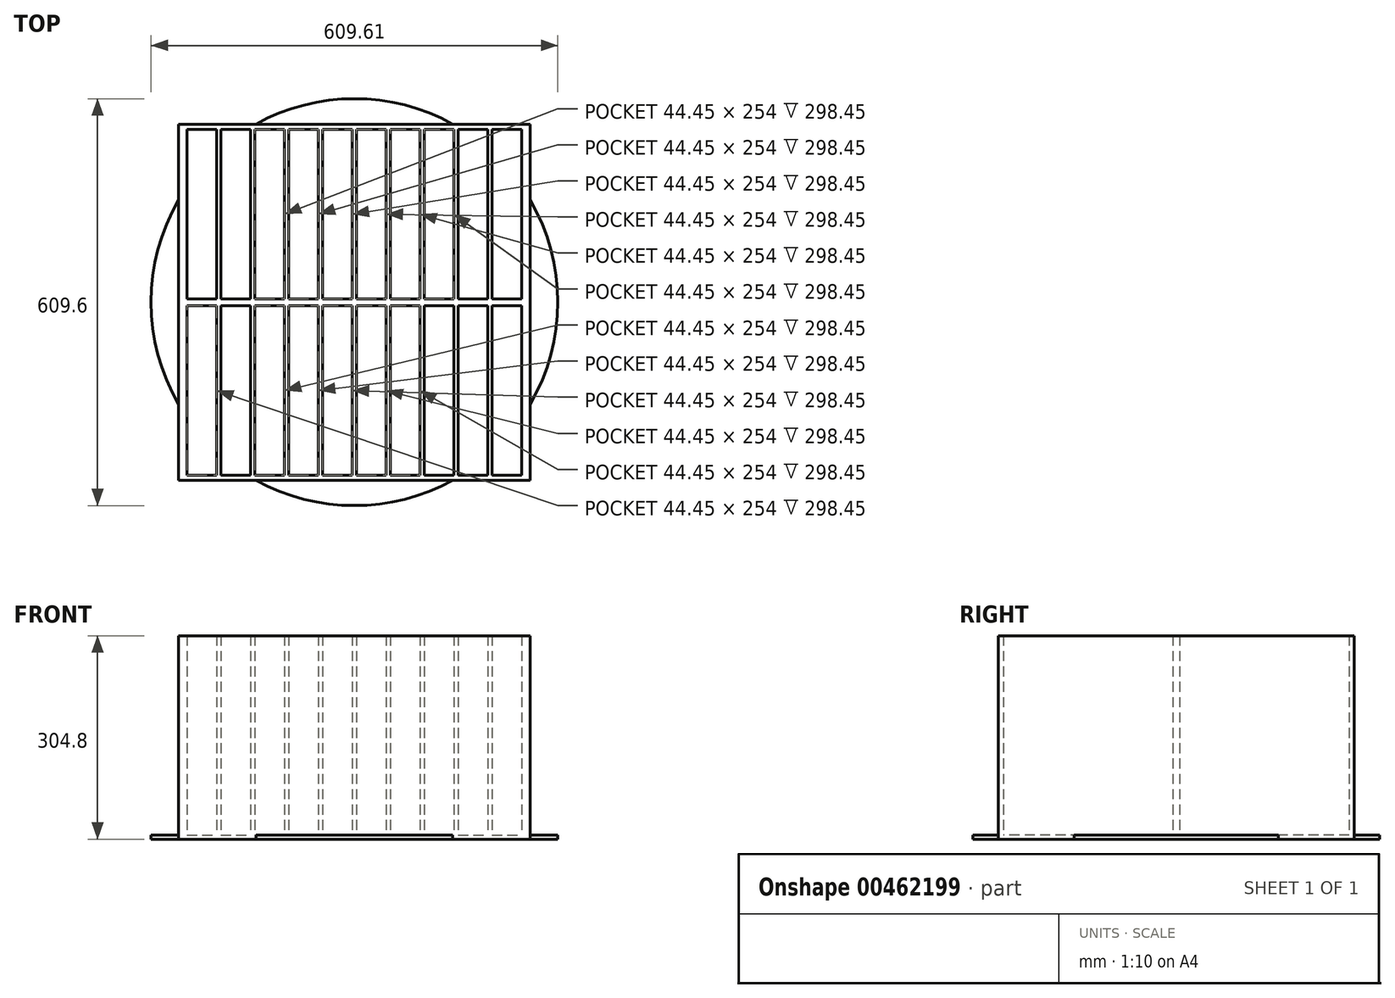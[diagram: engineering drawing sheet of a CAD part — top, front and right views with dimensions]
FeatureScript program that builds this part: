
annotation { "Feature Type Name" : "Feature", "Feature Type Description" : "" }
export const myFeature = defineFeature(function(context is Context, id is Id, definition is map)
    precondition{}
    {
        {
            var Q0;
            Q0=qCreatedBy(makeId("Top.planeOp"),FACE);
            var sketch = newSketch(context, id + "F0", { "sketchPlane" : qUnion([Q0])});
            skLineSegment(sketch, "E0.bottom", {"start": v(-260.35, 261.62) * mm, "end": v(266.7, 261.62) * mm});
            skLineSegment(sketch, "E0.top", {"start": v(-260.35, -271.78) * mm, "end": v(266.7, -271.78) * mm});
            skLineSegment(sketch, "E0.left", {"start": v(-260.35, 261.62) * mm, "end": v(-260.35, -271.78) * mm});
            skLineSegment(sketch, "E0.right", {"start": v(266.7, 261.62) * mm, "end": v(266.7, -271.78) * mm});
            skLineSegment(sketch, "E1.bottom", {"start": v(-247.65, 254) * mm, "end": v(-203.2, 254) * mm});
            skLineSegment(sketch, "E1.top", {"start": v(-247.65, 0) * mm, "end": v(-203.2, 0) * mm});
            skLineSegment(sketch, "E1.left", {"start": v(-247.65, 254) * mm, "end": v(-247.65, 0) * mm});
            skLineSegment(sketch, "E1.right", {"start": v(-203.2, 254) * mm, "end": v(-203.2, 0) * mm});
            skLineSegment(sketch, "E2.bottom", {"start": v(-196.85, 254) * mm, "end": v(-152.4, 254) * mm});
            skLineSegment(sketch, "E2.top", {"start": v(-196.85, 0) * mm, "end": v(-152.4, 0) * mm});
            skLineSegment(sketch, "E2.left", {"start": v(-196.85, 254) * mm, "end": v(-196.85, 0) * mm});
            skLineSegment(sketch, "E2.right", {"start": v(-152.4, 254) * mm, "end": v(-152.4, 0) * mm});
            skLineSegment(sketch, "E3.bottom", {"start": v(-146.05, 254) * mm, "end": v(-101.6, 254) * mm});
            skLineSegment(sketch, "E3.top", {"start": v(-146.05, 0) * mm, "end": v(-101.6, 0) * mm});
            skLineSegment(sketch, "E3.left", {"start": v(-146.05, 254) * mm, "end": v(-146.05, 0) * mm});
            skLineSegment(sketch, "E3.right", {"start": v(-101.6, 254) * mm, "end": v(-101.6, 0) * mm});
            skLineSegment(sketch, "E4.bottom", {"start": v(-95.25, 254) * mm, "end": v(-50.8, 254) * mm});
            skLineSegment(sketch, "E4.top", {"start": v(-95.25, 0) * mm, "end": v(-50.8, 0) * mm});
            skLineSegment(sketch, "E4.left", {"start": v(-95.25, 254) * mm, "end": v(-95.25, 0) * mm});
            skLineSegment(sketch, "E4.right", {"start": v(-50.8, 254) * mm, "end": v(-50.8, 0) * mm});
            skLineSegment(sketch, "E5.bottom", {"start": v(-44.45, 254) * mm, "end": v(0, 254) * mm});
            skLineSegment(sketch, "E5.top", {"start": v(-44.45, 0) * mm, "end": v(0, 0) * mm});
            skLineSegment(sketch, "E5.left", {"start": v(-44.45, 254) * mm, "end": v(-44.45, 0) * mm});
            skLineSegment(sketch, "E5.right", {"start": v(0, 254) * mm, "end": v(0, 0) * mm});
            skLineSegment(sketch, "E6.bottom", {"start": v(6.35, 254) * mm, "end": v(50.8, 254) * mm});
            skLineSegment(sketch, "E6.top", {"start": v(6.35, 0) * mm, "end": v(50.8, 0) * mm});
            skLineSegment(sketch, "E6.left", {"start": v(6.35, 254) * mm, "end": v(6.35, 0) * mm});
            skLineSegment(sketch, "E6.right", {"start": v(50.8, 254) * mm, "end": v(50.8, 0) * mm});
            skLineSegment(sketch, "E7.bottom", {"start": v(57.15, 254) * mm, "end": v(101.6, 254) * mm});
            skLineSegment(sketch, "E7.top", {"start": v(57.15, 0) * mm, "end": v(101.6, 0) * mm});
            skLineSegment(sketch, "E7.left", {"start": v(57.15, 254) * mm, "end": v(57.15, 0) * mm});
            skLineSegment(sketch, "E7.right", {"start": v(101.6, 254) * mm, "end": v(101.6, 0) * mm});
            skLineSegment(sketch, "E8.bottom", {"start": v(107.95, 254) * mm, "end": v(152.4, 254) * mm});
            skLineSegment(sketch, "E8.top", {"start": v(107.95, 0) * mm, "end": v(152.4, 0) * mm});
            skLineSegment(sketch, "E8.left", {"start": v(107.95, 254) * mm, "end": v(107.95, 0) * mm});
            skLineSegment(sketch, "E8.right", {"start": v(152.4, 254) * mm, "end": v(152.4, 0) * mm});
            skLineSegment(sketch, "E9.bottom", {"start": v(158.75, 254) * mm, "end": v(203.2, 254) * mm});
            skLineSegment(sketch, "E9.top", {"start": v(158.75, 0) * mm, "end": v(203.2, 0) * mm});
            skLineSegment(sketch, "E9.left", {"start": v(158.75, 254) * mm, "end": v(158.75, 0) * mm});
            skLineSegment(sketch, "E9.right", {"start": v(203.2, 254) * mm, "end": v(203.2, 0) * mm});
            skLineSegment(sketch, "E10.bottom", {"start": v(209.55, 254) * mm, "end": v(254, 254) * mm});
            skLineSegment(sketch, "E10.top", {"start": v(209.55, 0) * mm, "end": v(254, 0) * mm});
            skLineSegment(sketch, "E10.left", {"start": v(209.55, 254) * mm, "end": v(209.55, 0) * mm});
            skLineSegment(sketch, "E10.right", {"start": v(254, 254) * mm, "end": v(254, 0) * mm});
            skLineSegment(sketch, "E11.bottom", {"start": v(-247.65, -10.16) * mm, "end": v(-203.2, -10.16) * mm});
            skLineSegment(sketch, "E11.top", {"start": v(-247.65, -264.16) * mm, "end": v(-203.2, -264.16) * mm});
            skLineSegment(sketch, "E11.left", {"start": v(-247.65, -10.16) * mm, "end": v(-247.65, -264.16) * mm});
            skLineSegment(sketch, "E11.right", {"start": v(-203.2, -10.16) * mm, "end": v(-203.2, -264.16) * mm});
            skLineSegment(sketch, "E12.bottom", {"start": v(-196.85, -10.16) * mm, "end": v(-152.4, -10.16) * mm});
            skLineSegment(sketch, "E12.top", {"start": v(-196.85, -264.16) * mm, "end": v(-152.4, -264.16) * mm});
            skLineSegment(sketch, "E12.left", {"start": v(-196.85, -10.16) * mm, "end": v(-196.85, -264.16) * mm});
            skLineSegment(sketch, "E12.right", {"start": v(-152.4, -10.16) * mm, "end": v(-152.4, -264.16) * mm});
            skLineSegment(sketch, "E13.bottom", {"start": v(-146.05, -10.16) * mm, "end": v(-101.6, -10.16) * mm});
            skLineSegment(sketch, "E13.top", {"start": v(-146.05, -264.16) * mm, "end": v(-101.6, -264.16) * mm});
            skLineSegment(sketch, "E13.left", {"start": v(-146.05, -10.16) * mm, "end": v(-146.05, -264.16) * mm});
            skLineSegment(sketch, "E13.right", {"start": v(-101.6, -10.16) * mm, "end": v(-101.6, -264.16) * mm});
            skLineSegment(sketch, "E14.bottom", {"start": v(-95.25, -10.16) * mm, "end": v(-50.8, -10.16) * mm});
            skLineSegment(sketch, "E14.top", {"start": v(-95.25, -264.16) * mm, "end": v(-50.8, -264.16) * mm});
            skLineSegment(sketch, "E14.left", {"start": v(-95.25, -10.16) * mm, "end": v(-95.25, -264.16) * mm});
            skLineSegment(sketch, "E14.right", {"start": v(-50.8, -10.16) * mm, "end": v(-50.8, -264.16) * mm});
            skLineSegment(sketch, "E15.bottom", {"start": v(-44.45, -10.16) * mm, "end": v(0, -10.16) * mm});
            skLineSegment(sketch, "E15.top", {"start": v(-44.45, -264.16) * mm, "end": v(0, -264.16) * mm});
            skLineSegment(sketch, "E15.left", {"start": v(-44.45, -10.16) * mm, "end": v(-44.45, -264.16) * mm});
            skLineSegment(sketch, "E15.right", {"start": v(0, -10.16) * mm, "end": v(0, -264.16) * mm});
            skLineSegment(sketch, "E16.bottom", {"start": v(6.35, -10.16) * mm, "end": v(50.8, -10.16) * mm});
            skLineSegment(sketch, "E16.top", {"start": v(6.35, -264.16) * mm, "end": v(50.8, -264.16) * mm});
            skLineSegment(sketch, "E16.left", {"start": v(6.35, -10.16) * mm, "end": v(6.35, -264.16) * mm});
            skLineSegment(sketch, "E16.right", {"start": v(50.8, -10.16) * mm, "end": v(50.8, -264.16) * mm});
            skLineSegment(sketch, "E17.bottom", {"start": v(57.15, -10.16) * mm, "end": v(101.6, -10.16) * mm});
            skLineSegment(sketch, "E17.top", {"start": v(57.15, -264.16) * mm, "end": v(101.6, -264.16) * mm});
            skLineSegment(sketch, "E17.left", {"start": v(57.15, -10.16) * mm, "end": v(57.15, -264.16) * mm});
            skLineSegment(sketch, "E17.right", {"start": v(101.6, -10.16) * mm, "end": v(101.6, -264.16) * mm});
            skLineSegment(sketch, "E18.bottom", {"start": v(107.95, -10.16) * mm, "end": v(152.4, -10.16) * mm});
            skLineSegment(sketch, "E18.top", {"start": v(107.95, -264.16) * mm, "end": v(152.4, -264.16) * mm});
            skLineSegment(sketch, "E18.left", {"start": v(107.95, -10.16) * mm, "end": v(107.95, -264.16) * mm});
            skLineSegment(sketch, "E18.right", {"start": v(152.4, -10.16) * mm, "end": v(152.4, -264.16) * mm});
            skLineSegment(sketch, "E19.bottom", {"start": v(158.75, -10.16) * mm, "end": v(203.2, -10.16) * mm});
            skLineSegment(sketch, "E19.top", {"start": v(158.75, -264.16) * mm, "end": v(203.2, -264.16) * mm});
            skLineSegment(sketch, "E19.left", {"start": v(158.75, -10.16) * mm, "end": v(158.75, -264.16) * mm});
            skLineSegment(sketch, "E19.right", {"start": v(203.2, -10.16) * mm, "end": v(203.2, -264.16) * mm});
            skLineSegment(sketch, "E20.bottom", {"start": v(209.55, -10.16) * mm, "end": v(254, -10.16) * mm});
            skLineSegment(sketch, "E20.top", {"start": v(209.55, -264.16) * mm, "end": v(254, -264.16) * mm});
            skLineSegment(sketch, "E20.left", {"start": v(209.55, -10.16) * mm, "end": v(209.55, -264.16) * mm});
            skLineSegment(sketch, "E20.right", {"start": v(254, -10.16) * mm, "end": v(254, -264.16) * mm});
            skLineSegment(sketch, "E21", {"start": v(3.18, 261.62) * mm, "end": v(3.18, -271.78) * mm, "construction": true});
            skLineSegment(sketch, "E22", {"start": v(266.7, -5.08) * mm, "end": v(-260.35, -5.08) * mm, "construction": true});
            skCircle(sketch, "E23", {"center": v(3.18, -5.08) * mm, "radius": 304.8 * mm});
            skSolve(sketch);
        }
        {
            var Q0;
            {var subQ0=sQuery(id+"F0.wireOp",EDGE,"E11.top");Q0=makeQuery(id+"F0.imprint","IMPRINT",FACE,{"disambiguationData":[TD([[makeQuery(id+"F0.imprint","IMPRINT",EDGE,{"derivedFrom":subQ0}),-1.0]])]});}
            var Q1;
            {var subQ19=sQuery(id+"F0.wireOp",EDGE,"E1.top");Q1=makeQuery(id+"F0.imprint","IMPRINT",FACE,{"disambiguationData":[TD([[makeQuery(id+"F0.imprint","IMPRINT",EDGE,{"derivedFrom":subQ19}),-1.0]])]});}
            var Q2;
            {var subQ1=sQuery(id+"F0.wireOp",EDGE,"E1.bottom");Q2=makeQuery(id+"F0.imprint","IMPRINT",FACE,{"disambiguationData":[TD([[makeQuery(id+"F0.imprint","IMPRINT",EDGE,{"derivedFrom":subQ1}),1.0]])]});}
            var Q3;
            {var subQ13=sQuery(id+"F0.wireOp",EDGE,"E10.bottom");Q3=makeQuery(id+"F0.imprint","IMPRINT",FACE,{"disambiguationData":[TD([[makeQuery(id+"F0.imprint","IMPRINT",EDGE,{"derivedFrom":subQ13}),1.0]])]});}
            var Q4;
            {var subQ11=sQuery(id+"F0.wireOp",EDGE,"E20.top");Q4=makeQuery(id+"F0.imprint","IMPRINT",FACE,{"disambiguationData":[TD([[makeQuery(id+"F0.imprint","IMPRINT",EDGE,{"derivedFrom":subQ11}),-1.0]])]});}
            extrude(context, id + "F1", {"entities" : qUnion([Q0, Q1, Q2, Q3, Q4]), "depth" : 304.8 * mm, "offsetDistance" : 25.4 * mm});
        }
        {
            var Q0;
            {var subQ0=sQuery(id+"F0.wireOp",EDGE,"E23");var subQ1=sQuery(id+"F0.wireOp",EDGE,"E0.left");var subQ2=makeQuery(id+"F0.imprint","INTERSECT",VERTEX,{"disambiguationData":[OD(0.0)],"derivedFrom":[subQ1,subQ0]});Q0=makeQuery(id+"F0.imprint","IMPRINT",FACE,{"disambiguationData":[TD([[makeQuery(id+"F0.imprint","IMPRINT",EDGE,{"disambiguationData":[TD([[subQ2,-1.0]])],"derivedFrom":subQ1}),-1.0]])]});}
            var Q1;
            {var subQ19=sQuery(id+"F0.wireOp",EDGE,"E1.top");Q1=makeQuery(id+"F0.imprint","IMPRINT",FACE,{"disambiguationData":[TD([[makeQuery(id+"F0.imprint","IMPRINT",EDGE,{"derivedFrom":subQ19}),-1.0]])]});}
            var Q2;
            {var subQ0=sQuery(id+"F0.wireOp",EDGE,"E11.bottom");Q2=makeQuery(id+"F0.imprint","IMPRINT",FACE,{"disambiguationData":[TD([[makeQuery(id+"F0.imprint","IMPRINT",EDGE,{"derivedFrom":subQ0}),-1.0]])]});}
            var Q3;
            {var subQ1=sQuery(id+"F0.wireOp",EDGE,"E12.bottom");Q3=makeQuery(id+"F0.imprint","IMPRINT",FACE,{"disambiguationData":[TD([[makeQuery(id+"F0.imprint","IMPRINT",EDGE,{"derivedFrom":subQ1}),-1.0]])]});}
            var Q4;
            Q4=makeQuery(id+"F0.imprint","IMPRINT",FACE,{"disambiguationData":[TD([[makeQuery(id+"F0.imprint","IMPRINT",EDGE,{"derivedFrom":sQuery(id+"F0.wireOp",EDGE,"E13.bottom")}),-1.0]])]});
            var Q5;
            Q5=makeQuery(id+"F0.imprint","IMPRINT",FACE,{"disambiguationData":[TD([[makeQuery(id+"F0.imprint","IMPRINT",EDGE,{"derivedFrom":sQuery(id+"F0.wireOp",EDGE,"E14.bottom")}),-1.0]])]});
            var Q6;
            Q6=makeQuery(id+"F0.imprint","IMPRINT",FACE,{"disambiguationData":[TD([[makeQuery(id+"F0.imprint","IMPRINT",EDGE,{"derivedFrom":sQuery(id+"F0.wireOp",EDGE,"E15.bottom")}),-1.0]])]});
            var Q7;
            Q7=makeQuery(id+"F0.imprint","IMPRINT",FACE,{"disambiguationData":[TD([[makeQuery(id+"F0.imprint","IMPRINT",EDGE,{"derivedFrom":sQuery(id+"F0.wireOp",EDGE,"E16.bottom")}),-1.0]])]});
            var Q8;
            Q8=makeQuery(id+"F0.imprint","IMPRINT",FACE,{"disambiguationData":[TD([[makeQuery(id+"F0.imprint","IMPRINT",EDGE,{"derivedFrom":sQuery(id+"F0.wireOp",EDGE,"E17.bottom")}),-1.0]])]});
            var Q9;
            Q9=makeQuery(id+"F0.imprint","IMPRINT",FACE,{"disambiguationData":[TD([[makeQuery(id+"F0.imprint","IMPRINT",EDGE,{"derivedFrom":sQuery(id+"F0.wireOp",EDGE,"E18.bottom")}),-1.0]])]});
            var Q10;
            {var subQ1=sQuery(id+"F0.wireOp",EDGE,"E19.bottom");Q10=makeQuery(id+"F0.imprint","IMPRINT",FACE,{"disambiguationData":[TD([[makeQuery(id+"F0.imprint","IMPRINT",EDGE,{"derivedFrom":subQ1}),-1.0]])]});}
            var Q11;
            {var subQ0=sQuery(id+"F0.wireOp",EDGE,"E20.bottom");Q11=makeQuery(id+"F0.imprint","IMPRINT",FACE,{"disambiguationData":[TD([[makeQuery(id+"F0.imprint","IMPRINT",EDGE,{"derivedFrom":subQ0}),-1.0]])]});}
            var Q12;
            {var subQ0=sQuery(id+"F0.wireOp",EDGE,"E10.top");Q12=makeQuery(id+"F0.imprint","IMPRINT",FACE,{"disambiguationData":[TD([[makeQuery(id+"F0.imprint","IMPRINT",EDGE,{"derivedFrom":subQ0}),1.0]])]});}
            var Q13;
            {var subQ1=sQuery(id+"F0.wireOp",EDGE,"E9.top");Q13=makeQuery(id+"F0.imprint","IMPRINT",FACE,{"disambiguationData":[TD([[makeQuery(id+"F0.imprint","IMPRINT",EDGE,{"derivedFrom":subQ1}),1.0]])]});}
            var Q14;
            Q14=makeQuery(id+"F0.imprint","IMPRINT",FACE,{"disambiguationData":[TD([[makeQuery(id+"F0.imprint","IMPRINT",EDGE,{"derivedFrom":sQuery(id+"F0.wireOp",EDGE,"E8.bottom")}),-1.0]])]});
            var Q15;
            Q15=makeQuery(id+"F0.imprint","IMPRINT",FACE,{"disambiguationData":[TD([[makeQuery(id+"F0.imprint","IMPRINT",EDGE,{"derivedFrom":sQuery(id+"F0.wireOp",EDGE,"E7.bottom")}),-1.0]])]});
            var Q16;
            Q16=makeQuery(id+"F0.imprint","IMPRINT",FACE,{"disambiguationData":[TD([[makeQuery(id+"F0.imprint","IMPRINT",EDGE,{"derivedFrom":sQuery(id+"F0.wireOp",EDGE,"E6.bottom")}),-1.0]])]});
            var Q17;
            Q17=makeQuery(id+"F0.imprint","IMPRINT",FACE,{"disambiguationData":[TD([[makeQuery(id+"F0.imprint","IMPRINT",EDGE,{"derivedFrom":sQuery(id+"F0.wireOp",EDGE,"E5.bottom")}),-1.0]])]});
            var Q18;
            Q18=makeQuery(id+"F0.imprint","IMPRINT",FACE,{"disambiguationData":[TD([[makeQuery(id+"F0.imprint","IMPRINT",EDGE,{"derivedFrom":sQuery(id+"F0.wireOp",EDGE,"E3.bottom")}),-1.0]])]});
            var Q19;
            {var subQ2=sQuery(id+"F0.wireOp",EDGE,"E2.top");Q19=makeQuery(id+"F0.imprint","IMPRINT",FACE,{"disambiguationData":[TD([[makeQuery(id+"F0.imprint","IMPRINT",EDGE,{"derivedFrom":subQ2}),1.0]])]});}
            var Q20;
            {var subQ0=sQuery(id+"F0.wireOp",EDGE,"E1.top");Q20=makeQuery(id+"F0.imprint","IMPRINT",FACE,{"disambiguationData":[TD([[makeQuery(id+"F0.imprint","IMPRINT",EDGE,{"derivedFrom":subQ0}),1.0]])]});}
            var Q21;
            Q21=makeQuery(id+"F0.imprint","IMPRINT",FACE,{"disambiguationData":[TD([[makeQuery(id+"F0.imprint","IMPRINT",EDGE,{"derivedFrom":sQuery(id+"F0.wireOp",EDGE,"E4.bottom")}),-1.0]])]});
            var Q22;
            {var subQ0=sQuery(id+"F0.wireOp",EDGE,"E23");var subQ1=sQuery(id+"F0.wireOp",EDGE,"E0.top");var subQ2=makeQuery(id+"F0.imprint","INTERSECT",VERTEX,{"disambiguationData":[OD(0.0)],"derivedFrom":[subQ1,subQ0]});Q22=makeQuery(id+"F0.imprint","IMPRINT",FACE,{"disambiguationData":[TD([[makeQuery(id+"F0.imprint","IMPRINT",EDGE,{"disambiguationData":[TD([[subQ2,-1.0]])],"derivedFrom":subQ1}),-1.0]])]});}
            var Q23;
            {var subQ0=sQuery(id+"F0.wireOp",EDGE,"E23");var subQ1=sQuery(id+"F0.wireOp",EDGE,"E0.right");var subQ2=makeQuery(id+"F0.imprint","INTERSECT",VERTEX,{"disambiguationData":[OD(0.0)],"derivedFrom":[subQ1,subQ0]});Q23=makeQuery(id+"F0.imprint","IMPRINT",FACE,{"disambiguationData":[TD([[makeQuery(id+"F0.imprint","IMPRINT",EDGE,{"disambiguationData":[TD([[subQ2,-1.0]])],"derivedFrom":subQ1}),1.0]])]});}
            var Q24;
            {var subQ0=sQuery(id+"F0.wireOp",EDGE,"E23");var subQ1=sQuery(id+"F0.wireOp",EDGE,"E0.bottom");var subQ2=makeQuery(id+"F0.imprint","INTERSECT",VERTEX,{"disambiguationData":[OD(0.0)],"derivedFrom":[subQ1,subQ0]});Q24=makeQuery(id+"F0.imprint","IMPRINT",FACE,{"disambiguationData":[TD([[makeQuery(id+"F0.imprint","IMPRINT",EDGE,{"disambiguationData":[TD([[subQ2,-1.0]])],"derivedFrom":subQ1}),1.0]])]});}
            var Q25;
            {var subQ0=sQuery(id+"F0.wireOp",EDGE,"E19.right");var subQ1=sQuery(id+"F0.wireOp",EDGE,"E19.top");var subQ2=makeQuery(id+"F0.imprint","INTERSECT",VERTEX,{"derivedFrom":[subQ1,subQ0]});Q25=makeQuery(id+"F0.imprint","IMPRINT",FACE,{"disambiguationData":[TD([[makeQuery(id+"F0.imprint","IMPRINT",EDGE,{"disambiguationData":[TD([[subQ2,1.0]])],"derivedFrom":subQ1}),1.0]])]});}
            var Q26;
            {var subQ0=sQuery(id+"F0.wireOp",EDGE,"E11.top");Q26=makeQuery(id+"F0.imprint","IMPRINT",FACE,{"disambiguationData":[TD([[makeQuery(id+"F0.imprint","IMPRINT",EDGE,{"derivedFrom":subQ0}),1.0]])]});}
            var Q27;
            {var subQ0=sQuery(id+"F0.wireOp",EDGE,"E12.left");var subQ1=sQuery(id+"F0.wireOp",EDGE,"E12.top");var subQ2=makeQuery(id+"F0.imprint","INTERSECT",VERTEX,{"derivedFrom":[subQ1,subQ0]});Q27=makeQuery(id+"F0.imprint","IMPRINT",FACE,{"disambiguationData":[TD([[makeQuery(id+"F0.imprint","IMPRINT",EDGE,{"disambiguationData":[TD([[subQ2,-1.0]])],"derivedFrom":subQ1}),1.0]])]});}
            var Q28;
            {var subQ0=sQuery(id+"F0.wireOp",EDGE,"E20.top");Q28=makeQuery(id+"F0.imprint","IMPRINT",FACE,{"disambiguationData":[TD([[makeQuery(id+"F0.imprint","IMPRINT",EDGE,{"derivedFrom":subQ0}),1.0]])]});}
            var Q29;
            {var subQ0=sQuery(id+"F0.wireOp",EDGE,"E10.bottom");Q29=makeQuery(id+"F0.imprint","IMPRINT",FACE,{"disambiguationData":[TD([[makeQuery(id+"F0.imprint","IMPRINT",EDGE,{"derivedFrom":subQ0}),-1.0]])]});}
            var Q30;
            {var subQ0=sQuery(id+"F0.wireOp",EDGE,"E9.right");var subQ1=sQuery(id+"F0.wireOp",EDGE,"E9.bottom");var subQ2=makeQuery(id+"F0.imprint","INTERSECT",VERTEX,{"derivedFrom":[subQ1,subQ0]});Q30=makeQuery(id+"F0.imprint","IMPRINT",FACE,{"disambiguationData":[TD([[makeQuery(id+"F0.imprint","IMPRINT",EDGE,{"disambiguationData":[TD([[subQ2,1.0]])],"derivedFrom":subQ1}),-1.0]])]});}
            var Q31;
            {var subQ0=sQuery(id+"F0.wireOp",EDGE,"E2.left");var subQ1=sQuery(id+"F0.wireOp",EDGE,"E2.bottom");var subQ2=makeQuery(id+"F0.imprint","INTERSECT",VERTEX,{"derivedFrom":[subQ1,subQ0]});Q31=makeQuery(id+"F0.imprint","IMPRINT",FACE,{"disambiguationData":[TD([[makeQuery(id+"F0.imprint","IMPRINT",EDGE,{"disambiguationData":[TD([[subQ2,-1.0]])],"derivedFrom":subQ1}),-1.0]])]});}
            var Q32;
            {var subQ0=sQuery(id+"F0.wireOp",EDGE,"E1.bottom");Q32=makeQuery(id+"F0.imprint","IMPRINT",FACE,{"disambiguationData":[TD([[makeQuery(id+"F0.imprint","IMPRINT",EDGE,{"derivedFrom":subQ0}),-1.0]])]});}
            extrude(context, id + "F2", {"entities" : qUnion([Q0, Q1, Q2, Q3, Q4, Q5, Q6, Q7, Q8, Q9, Q10, Q11, Q12, Q13, Q14, Q15, Q16, Q17, Q18, Q19, Q20, Q21, Q22, Q23, Q24, Q25, Q26, Q27, Q28, Q29, Q30, Q31, Q32]), "operationType" : NewBodyOperationType.ADD, "depth" : 6.35 * mm, "offsetDistance" : 25.4 * mm});
        }
    });
